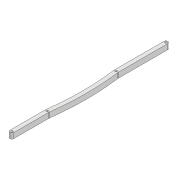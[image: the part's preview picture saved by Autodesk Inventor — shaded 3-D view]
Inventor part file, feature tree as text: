
AUTODESK INVENTOR PART (.ipt)
format: ipt  version: 2022 (Build 260153000, 153)  size: 113,152 bytes
history: native  units: mm
features: extrude x1, other x1, fillet x1, sketch x1
ambient origin geometry x8: Origin, YZ Plane, XZ Plane, XY Plane, X Axis, Y Axis, Z Axis, Center Point
bodies: Solid1 (feature_tree)
feature tree (4):
  extrude  "Extrusion1"  Depth=6.0mm
  other  "Work Axis1"
  fillet  "Fillet1"  Radius=3.0mm
  sketch  "Sketch1"  dims[d0=233.87mm d1=6.0mm d2=3.0mm d3=3.0mm d4=8.0mm d5=0.0mm d6=3.0mm d7=158.374mm d8=3.0mm d9=53.738mm d10=400.0mm d11=400.0mm d12=10.0mm]
